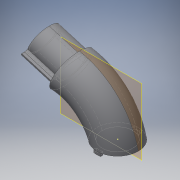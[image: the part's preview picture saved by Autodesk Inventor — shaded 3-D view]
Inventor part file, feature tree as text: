
AUTODESK INVENTOR PART (.ipt)
format: ipt  version: 2016 (Build 200138000, 138)  size: 356,864 bytes
history: native  units: mm
features: sketch x13, sweep x5, fillet x4, extrude x2, other x1
ambient origin geometry x8: Origin, YZ Plane, XZ Plane, XY Plane, X Axis, Y Axis, Z Axis, Center Point
bodies: Solide1 (feature_tree)
feature tree (25):
  sweep  "Balayage1"
  extrude  "Extrusion1"  Depth=27.0mm
  sketch  "Esquisse4"
  other  "Plan de construction1"
  sweep  "Balayage2"
  extrude  "Extrusion2"  Depth=2.0mm TaperAngle=0.0deg
  sketch  "Esquisse7"
  sweep  "Balayage3"
  sweep  "Balayage4"
  sweep  "Balayage5"
  fillet  "Congé1"  Radius=1.95mm
  fillet  "Congé2"  Radius=20.0mm
  fillet  "Congé3"  [1 undecoded]
  fillet  "Congé4"  Radius=17.0mm
  sketch  "Esquisse1"
  sketch  "Esquisse2"
  sketch  "Esquisse3"
  sketch  "Esquisse5"
  sketch  "Esquisse6"
  sketch  "Esquisse8"
  sketch  "Esquisse9"
  sketch  "Esquisse10"
  sketch  "Esquisse11"
  sketch  "Esquisse12"
  sketch  "Esquisse13"
note: 1 required parameter value undecoded (feature->parameter linkage not recoverable at this tier; creation-order binding heuristic only, values carry confidence <= 0.55)
